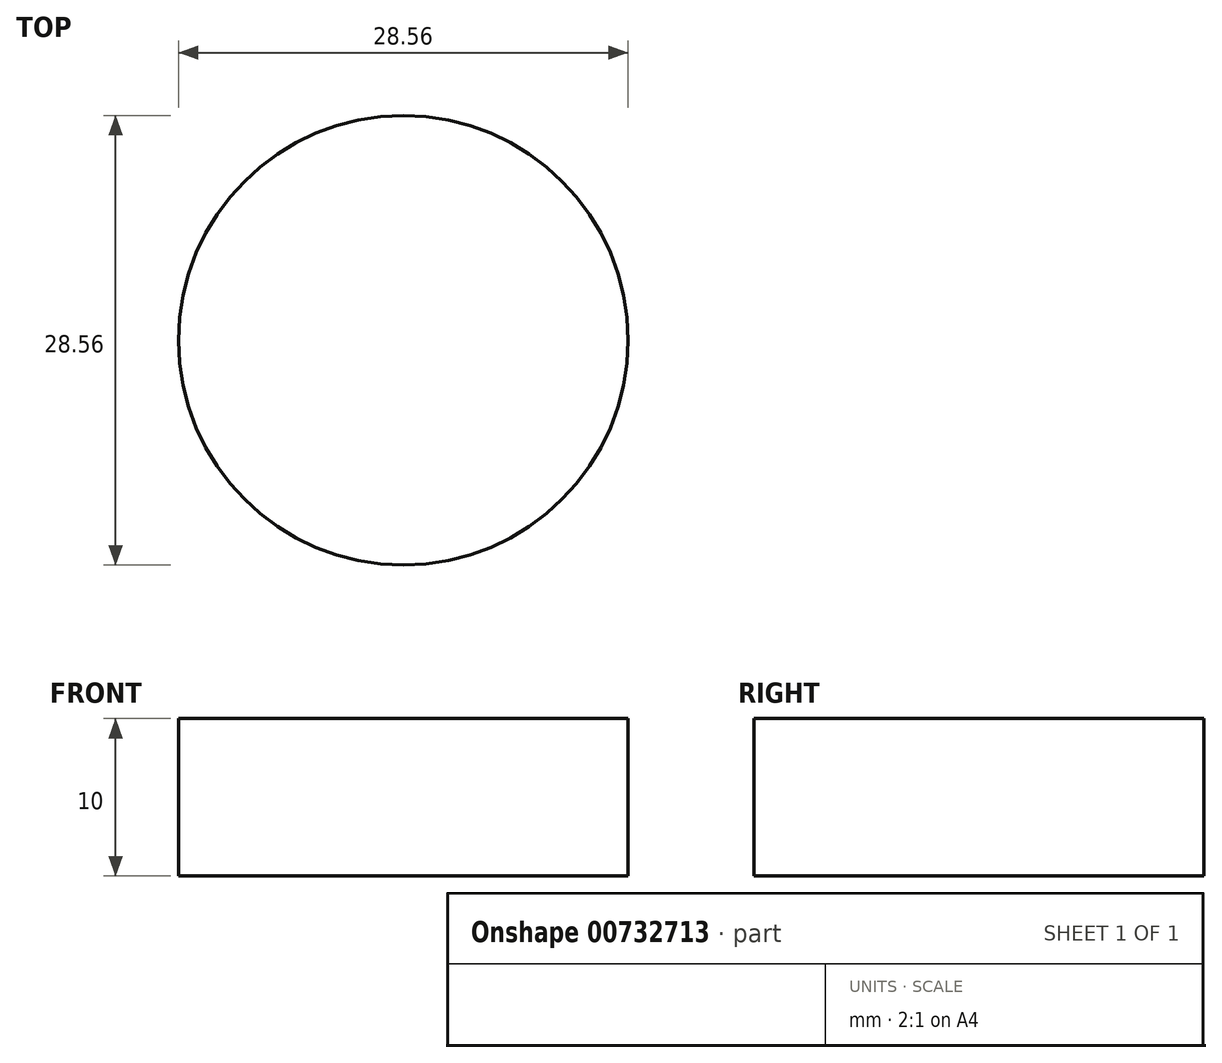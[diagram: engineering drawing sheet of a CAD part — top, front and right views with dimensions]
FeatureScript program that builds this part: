
annotation { "Feature Type Name" : "Feature", "Feature Type Description" : "" }
export const myFeature = defineFeature(function(context is Context, id is Id, definition is map)
    precondition{}
    {
        {
            var Q0;
            Q0=qCreatedBy(makeId("Top.planeOp"),FACE);
            var sketch = newSketch(context, id + "F0", { "sketchPlane" : qUnion([Q0])});
            skCircle(sketch, "E0", {"center": v(0, 0) * mm, "radius": 14.28 * mm});
            skSolve(sketch);
        }
        {
            var Q0;
            Q0=qSketchRegion(id+"F0",true);
            extrude(context, id + "F1", {"entities" : qUnion([Q0]), "depth" : 10 * mm, "offsetDistance" : 25 * mm});
        }
    });
